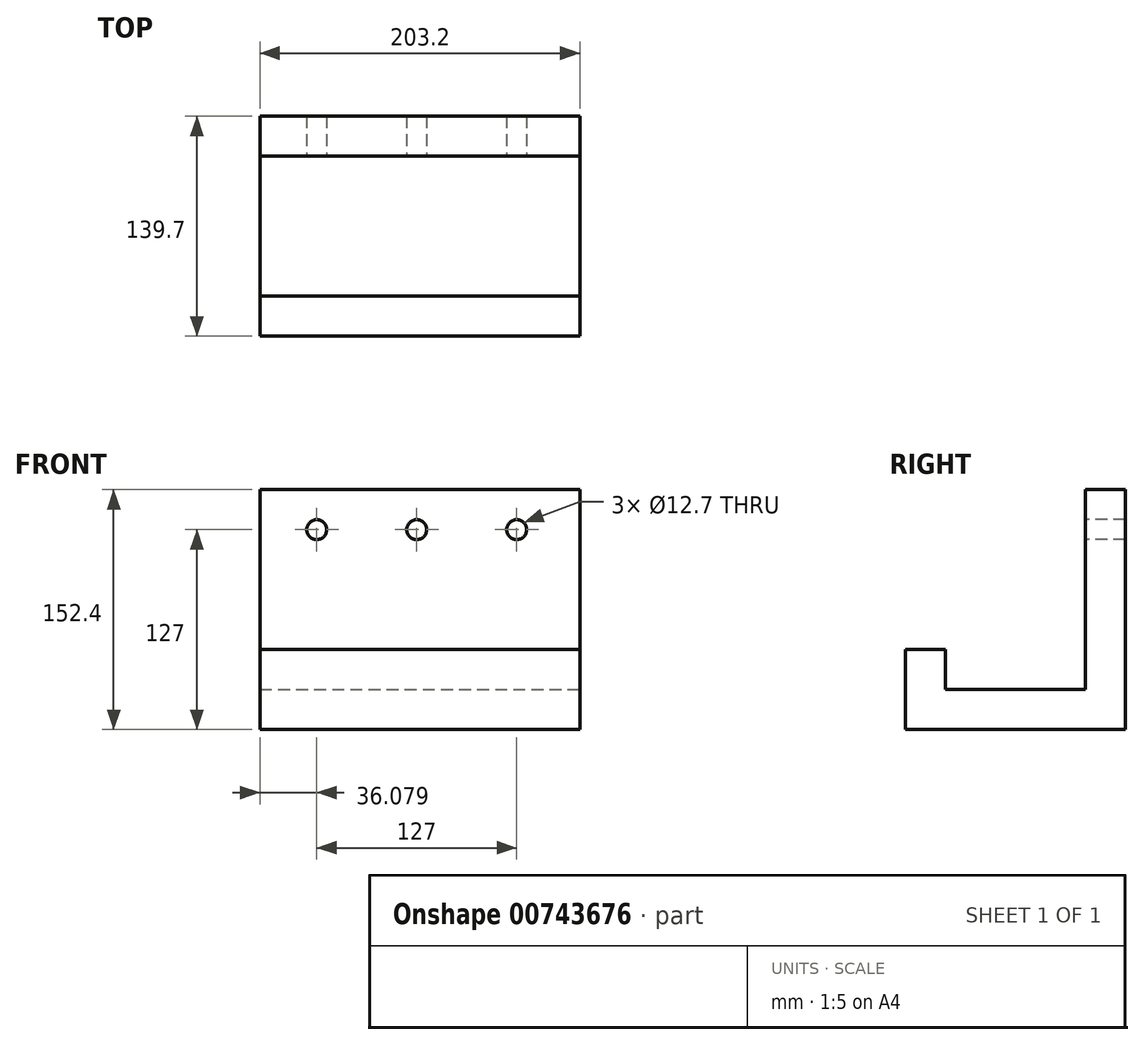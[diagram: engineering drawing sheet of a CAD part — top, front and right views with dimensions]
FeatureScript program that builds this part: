
annotation { "Feature Type Name" : "Feature", "Feature Type Description" : "" }
export const myFeature = defineFeature(function(context is Context, id is Id, definition is map)
    precondition{}
    {
        {
            var Q0;
            Q0=qCreatedBy(makeId("Right.planeOp"),FACE);
            var sketch = newSketch(context, id + "F0", { "sketchPlane" : qUnion([Q0])});
            skLineSegment(sketch, "E0", {"start": v(0, 0) * mm, "end": v(-139.7, 0) * mm});
            skLineSegment(sketch, "E1", {"start": v(-139.7, 0) * mm, "end": v(-139.7, 50.8) * mm});
            skLineSegment(sketch, "E2", {"start": v(-139.7, 50.8) * mm, "end": v(-114.3, 50.8) * mm});
            skLineSegment(sketch, "E3", {"start": v(-114.3, 50.8) * mm, "end": v(-114.3, 25.4) * mm});
            skLineSegment(sketch, "E4", {"start": v(-114.3, 25.4) * mm, "end": v(-25.4, 25.4) * mm});
            skLineSegment(sketch, "E5", {"start": v(-25.4, 25.4) * mm, "end": v(-25.4, 152.4) * mm});
            skLineSegment(sketch, "E6", {"start": v(-25.4, 152.4) * mm, "end": v(0, 152.4) * mm});
            skLineSegment(sketch, "E7", {"start": v(0, 152.4) * mm, "end": v(0, 0) * mm});
            skSolve(sketch);
        }
        {
            var Q0;
            Q0 = qSketchRegion(id + "F0", true);
            extrude(context, id + "F1", {"entities" : qUnion([Q0]), "oppositeDirection" : true, "depth" : 203.2 * mm, "offsetDistance" : 25.4 * mm});
        }
        {
            var Q0;
            Q0=makeQuery(id+"F1.opExtrude","SWEPT_FACE",FACE,{"disambiguationData":[OSD([sQuery(id+"F0.wireOp",EDGE,"E5")])]});
            var sketch = newSketch(context, id + "F2", { "sketchPlane" : qUnion([Q0])});
            skPoint(sketch, "E8", {"position": v(-167.12, 127) * mm});
            skPoint(sketch, "E9", {"position": v(-103.62, 127) * mm});
            skPoint(sketch, "E10", {"position": v(-40.12, 127) * mm});
            skSolve(sketch);
        }
        {
            var Q0;
            Q0=sQuery(id+"F2.wireOp",VERTEX,"E8");
            var Q1;
            Q1=sQuery(id+"F2.wireOp",VERTEX,"E9");
            var Q2;
            Q2=sQuery(id+"F2.wireOp",VERTEX,"E10");
            var Q3;
            Q3=makeQuery(id+"F1.opExtrude","SWEPT_BODY",BODY,{"disambiguationData":[OSD([sQuery(id+"F0.wireOp",EDGE,"E0"),sQuery(id+"F0.wireOp",EDGE,"E1"),sQuery(id+"F0.wireOp",EDGE,"E2"),sQuery(id+"F0.wireOp",EDGE,"E3"),sQuery(id+"F0.wireOp",EDGE,"E4"),sQuery(id+"F0.wireOp",EDGE,"E5"),sQuery(id+"F0.wireOp",EDGE,"E6"),sQuery(id+"F0.wireOp",EDGE,"E7")])]});
            hole(context, id + "F3", {"style" : HoleStyle.SIMPLE, "endStyle" : HoleEndStyle.THROUGH, "holeDiameter" : 12.7 * mm, "majorDiameter" : 6.35 * mm, "isTappedThrough" : true, "tappedDepth" : 12.7 * mm, "tapClearance" : 3, "locations" : qUnion([Q0, Q1, Q2]), "scope" : qUnion([Q3])});
        }
    });
